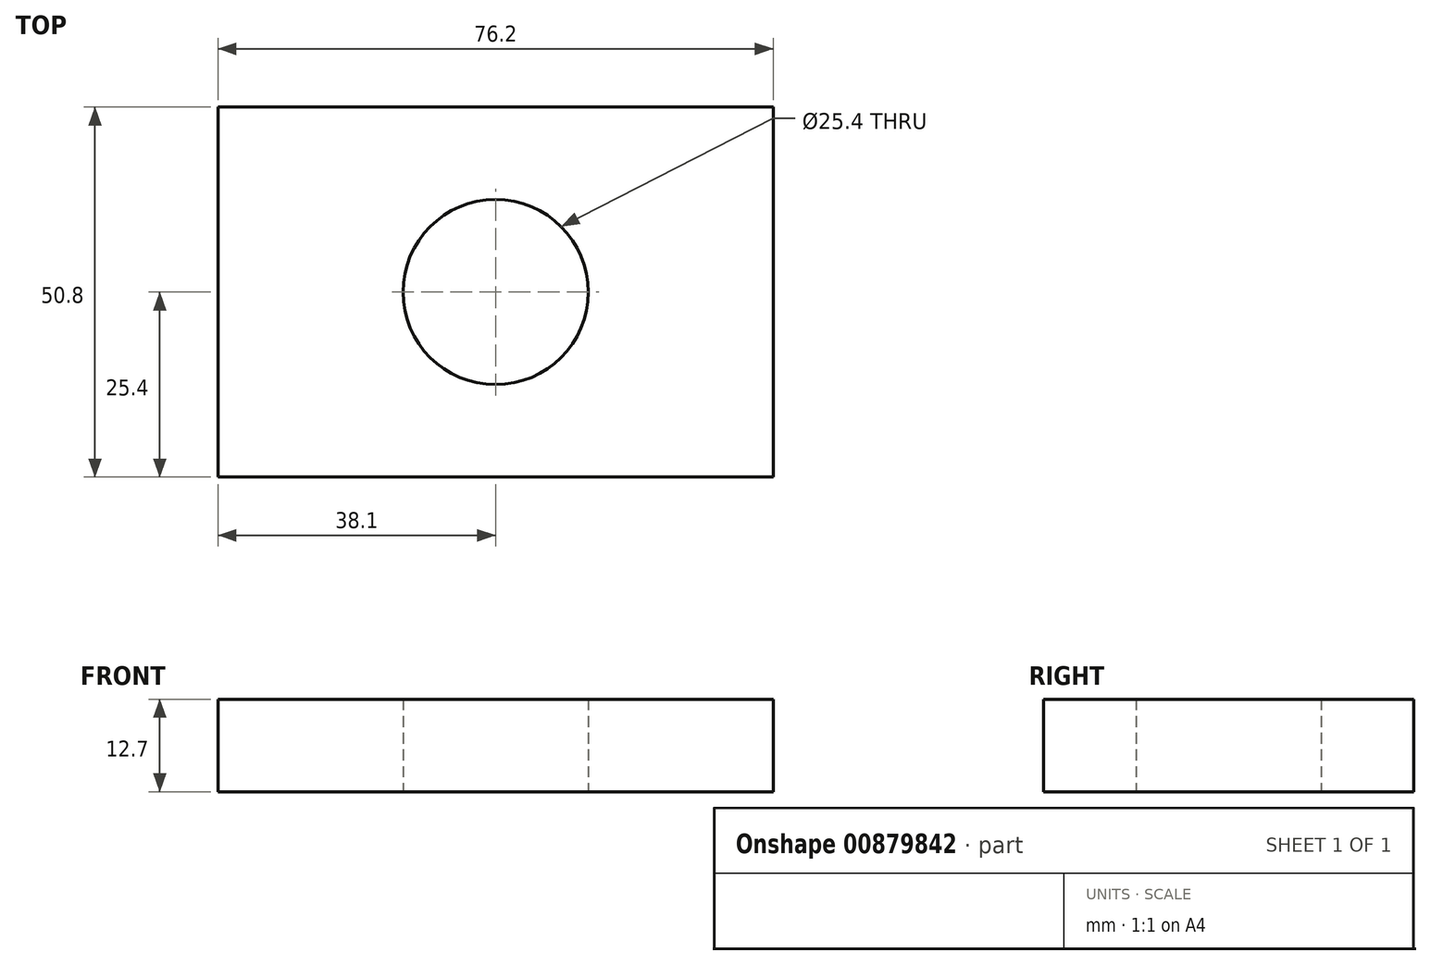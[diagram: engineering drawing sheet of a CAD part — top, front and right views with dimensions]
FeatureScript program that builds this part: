
annotation { "Feature Type Name" : "Feature", "Feature Type Description" : "" }
export const myFeature = defineFeature(function(context is Context, id is Id, definition is map)
    precondition{}
    {
        {
            var Q0;
            Q0=qCreatedBy(makeId("Top.planeOp"),FACE);
            var sketch = newSketch(context, id + "F0", { "sketchPlane" : qUnion([Q0])});
            skLineSegment(sketch, "E0.bottom", {"start": v(38.1, -25.4) * mm, "end": v(-38.1, -25.4) * mm});
            skLineSegment(sketch, "E0.top", {"start": v(38.1, 25.4) * mm, "end": v(-38.1, 25.4) * mm});
            skLineSegment(sketch, "E0.left", {"start": v(38.1, -25.4) * mm, "end": v(38.1, 25.4) * mm});
            skLineSegment(sketch, "E0.right", {"start": v(-38.1, -25.4) * mm, "end": v(-38.1, 25.4) * mm});
            skPoint(sketch, "E0.middle", {"position": v(0, 0) * mm});
            skCircle(sketch, "E1", {"center": v(0, 0) * mm, "radius": 12.7 * mm});
            skSolve(sketch);
        }
        {
            var Q0;
            Q0=makeQuery(id+"F0.imprint","IMPRINT",FACE,{"disambiguationData":[TD([[makeQuery(id+"F0.imprint","IMPRINT",EDGE,{"derivedFrom":sQuery(id+"F0.wireOp",EDGE,"E0.bottom")}),-1.0]])]});
            extrude(context, id + "F1", {"entities" : qUnion([Q0]), "depth" : 12.7 * mm, "offsetDistance" : 25 * mm});
        }
    });
